# Revit family: REY-2-xxFSWxxxRAxxx
name_source: partatom
category: Oprawy oświetleniowe
revit_build: Autodesk Revit 2017 (Build: 20190507_1515(x64)
units: mm (PartAtom-declared; Revit-internal decimal feet)

## family parameters
Numer OmniClass = 23.80.70.11
Obiekt nadrzędny = Powierzchnia
Punkt obliczania pomieszczeń = Nie
Tnij formami wycięć po wczytaniu = Nie
Typ części = Normalny
Tytuł OmniClass = Luminaries for Internal Lighting
Współdzielony = Nie
Wymiar okrągłego złącza = Użyj średnicy
Źródło światła = Tak

## types (6) — shared parameters
Emituj kształt widoczny w renderingu = Nie
Emituj z długości prostokąta = 50 mm  [stored 0.164042 ft]
Emituj z szerokości prostokąta = 221 mm  [stored 0.725066 ft]
Filtr koloru = 16777215
Kod zespołu = D5020200
Lampa = LED
Obciążenie pozorne = 51 VA
Odchylenie kierunku = 90.00°
Plik sieci fotometrycznej = REY-2 50g.IES
Producent = RIDI Leuchten GmbH
URL = www.ridi.de
Zmiana temperatury barwowej przyciemniania lampy = <Brak>
brand = RIDI
conformity mark = CE
electrical safety class = 1
height = 149 mm  [stored 0.488845 ft]
ingress protection (IP) code = IP20
length = 270 mm  [stored 0.885827 ft]
nominal frequency = 50-60Hz
nominal voltage = 230
rated input power = 51
voltage type (AC, DC, UC) = AC
weight = 3,2 kg
width = 108 mm  [stored 0.354331 ft]
zero-valued in all types: Domyślna rzędna

## per-type parameters (varying)
| type | Model |
| REY-2 NDFSW830RA1300 | 0322039AQ |
| REY-2 DAFSW830RA1300 | 0332039AQ |
| REY-2 NDFSW840RA1300 | 0322040AQ |
| REY-2 DAFSW840RA1300 | 0332040AQ |
| REY-2 NDFSW930RA1100 | 0322043AQ |
| REY-2 DAFSW930RA1100 | 0332043AQ |

note: column(s) folded — value = type name in every type: product name

note: [stored X ft] marks values corroborated as IEEE doubles in the binary element streams (Revit-internal decimal feet)
